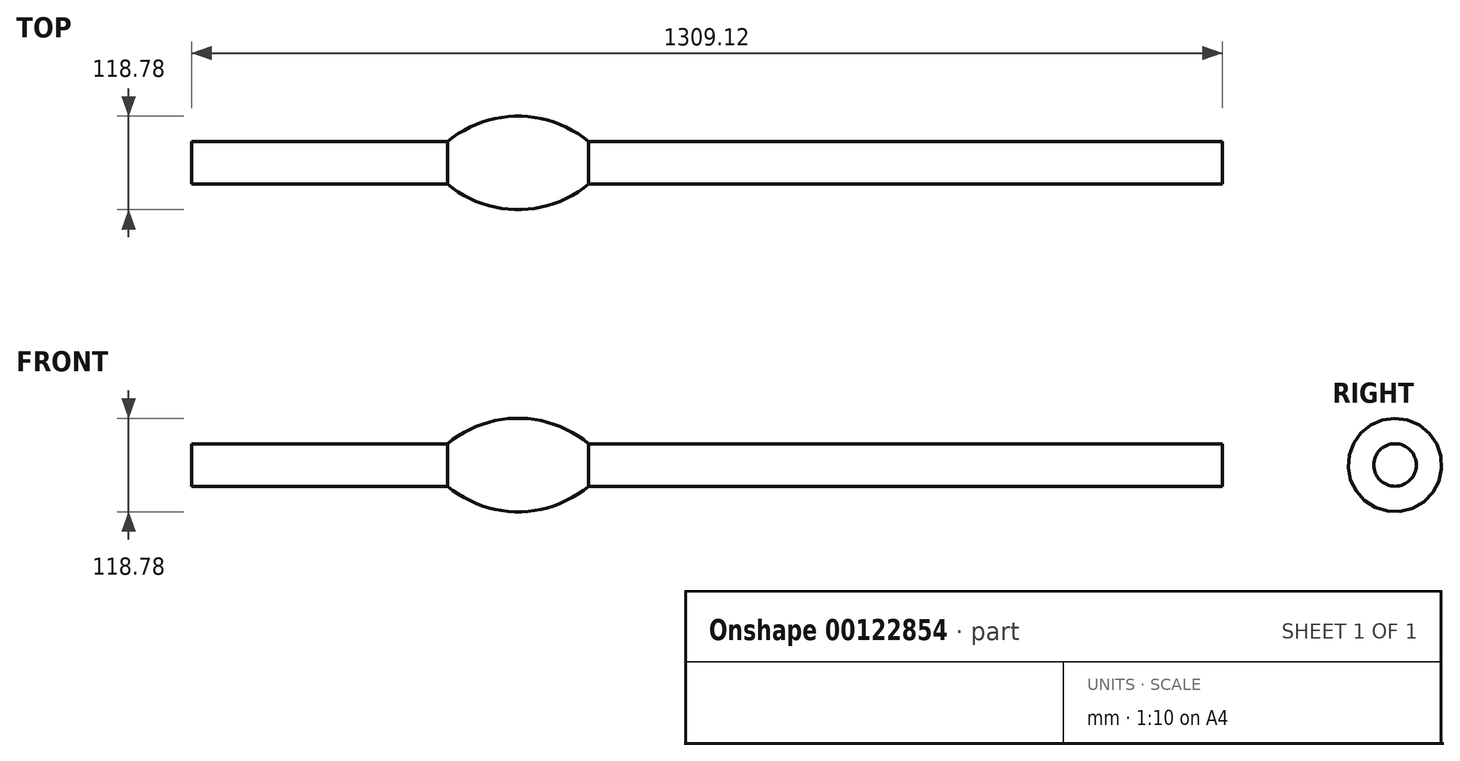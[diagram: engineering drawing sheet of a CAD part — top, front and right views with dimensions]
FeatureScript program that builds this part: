
annotation { "Feature Type Name" : "Feature", "Feature Type Description" : "" }
export const myFeature = defineFeature(function(context is Context, id is Id, definition is map)
    precondition{}
    {
        {
            var Q0;
            Q0=qCreatedBy(makeId("Front.planeOp"),FACE);
            var sketch = newSketch(context, id + "F0", { "sketchPlane" : qUnion([Q0])});
            skLineSegment(sketch, "E0", {"start": v(0, 0) * mm, "end": v(400, 0) * mm});
            skPoint(sketch, "E1.start.orphan", {"position": v(360, 0) * mm});
            skArc(sketch, "E2", {"start": v(579.12, 0) * mm, "mid": v(489.56, 32.4) * mm, "end": v(400, 0) * mm});
            skLineSegment(sketch, "E3", {"start": v(579.12, 0) * mm, "end": v(1079.12, 0) * mm});
            skLineSegment(sketch, "E4", {"start": v(0, 0) * mm, "end": v(0, -27) * mm});
            skPoint(sketch, "E5.end.orphan", {"position": v(1079.12, -27) * mm});
            skLineSegment(sketch, "E6", {"start": v(0, -27) * mm, "end": v(1079.12, -27) * mm});
            skLineSegment(sketch, "E7", {"start": v(1079.12, 0) * mm, "end": v(1079.12, -27) * mm});
            skSolve(sketch);
        }
        {
            var Q0;
            Q0=makeQuery(id+"F0.imprint","IMPRINT",FACE,{"disambiguationData":[TD([[makeQuery(id+"F0.imprint","IMPRINT",EDGE,{"derivedFrom":sQuery(id+"F0.wireOp",EDGE,"E0")}),-1.0]])]});
            var Q1;
            Q1=sQuery(id+"F0.wireOp",EDGE,"E6");
            revolve(context, id + "F1", {"entities" : qUnion([Q0]), "axis" : qUnion([Q1]), "revolveType" : RevolveType.FULL});
        }
        {
            var Q0;
            Q0=makeQuery(id+"F1.opRevolve","SWEPT_FACE",FACE,{"disambiguationData":[OSD([sQuery(id+"F0.wireOp",EDGE,"E7")])]});
            extrude(context, id + "F2", {"entities" : qUnion([Q0]), "operationType" : NewBodyOperationType.ADD, "depth" : 305 * mm});
        }
        {
            var Q0;
            Q0=makeQuery(id+"F1.opRevolve","SWEPT_FACE",FACE,{"disambiguationData":[OSD([sQuery(id+"F0.wireOp",EDGE,"E4")])]});
            extrude(context, id + "F3", {"entities" : qUnion([Q0]), "operationType" : NewBodyOperationType.REMOVE, "oppositeDirection" : true, "depth" : 75 * mm});
        }
    });
